annotation { "Feature Type Name" : "Feature", "Feature Type Description" : "" }
export const myFeature = defineFeature(function(context is Context, id is Id, definition is map)
    precondition{}
    {
        {
            var Q0;
            Q0=qCreatedBy(makeId("Top.planeOp"),FACE);
            var sketch = newSketch(context, id + "F0", { "sketchPlane" : qUnion([Q0])});
            skLineSegment(sketch, "E0.bottom", {"start": v(0, 0) * mm, "end": v(9, 0) * mm});
            skLineSegment(sketch, "E0.top", {"start": v(0, -17) * mm, "end": v(9, -17) * mm});
            skLineSegment(sketch, "E0.left", {"start": v(0, 0) * mm, "end": v(0, -17) * mm});
            skLineSegment(sketch, "E0.right", {"start": v(9, 0) * mm, "end": v(9, -17) * mm});
            skSolve(sketch);
        }
        {
            var Q0;
            Q0=makeQuery(id+"F0.imprint","IMPRINT",FACE,{"disambiguationData":[TD([[makeQuery(id+"F0.imprint","IMPRINT",EDGE,{"derivedFrom":sQuery(id+"F0.wireOp",EDGE,"E0.bottom")}),-1.0]])]});
            var Q1;
            Q1=sQuery(id+"F0.wireOp",EDGE,"E0.bottom");
            revolve(context, id + "F1", {"entities" : qUnion([Q0]), "axis" : qUnion([Q1]), "revolveType" : RevolveType.TWO_DIRECTIONS, "angle" : 0.56 * degree, "angleBack" : 0.1 * degree});
        }
        {
            var Q0;
            Q0=makeQuery(id+"F1.opRevolve","SWEPT_EDGE",EDGE,{"disambiguationData":[OSD([sQuery(id+"F0.wireOp",EDGE,"E0.top"),sQuery(id+"F0.wireOp",EDGE,"E0.left")])]});
            var Q1;
            Q1=makeQuery(id+"F1.opRevolve","SWEPT_EDGE",EDGE,{"disambiguationData":[OSD([sQuery(id+"F0.wireOp",EDGE,"E0.top"),sQuery(id+"F0.wireOp",EDGE,"E0.right")])]});
            chamfer(context, id + "F2", {"entities" : qUnion([Q0, Q1]), "chamferType" : ChamferType.OFFSET_ANGLE, "width" : 2 * mm, "oppositeDirection" : false, "angle" : 45 * degree, "tangentPropagation" : true});
        }
        {
            var Q0;
            Q0=sQuery(id+"F0.wireOp",VERTEX,"E0.left.end");
            var Q1;
            Q1=qCreatedBy(makeId("Front.planeOp"),FACE);
            cPlane(context, id + "F3", {"entities" : qUnion([Q0, Q1]), "cplaneType" : CPlaneType.PLANE_POINT, "offset" : 25 * mm, "width" : 150 * mm, "height" : 150 * mm});
        }
        {
            var Q0;
            Q0=qCreatedBy(id+"F3.planeOp",FACE);
            var sketch = newSketch(context, id + "F4", { "sketchPlane" : qUnion([Q0])});
            skLineSegment(sketch, "E1.bottom", {"start": v(2.01, -0.17) * mm, "end": v(2.11, -0.17) * mm});
            skLineSegment(sketch, "E1.top", {"start": v(2.01, -0.07) * mm, "end": v(2.11, -0.07) * mm});
            skLineSegment(sketch, "E1.left", {"start": v(2.01, -0.17) * mm, "end": v(2.01, -0.07) * mm});
            skLineSegment(sketch, "E1.right", {"start": v(2.11, -0.17) * mm, "end": v(2.11, -0.07) * mm});
            skLineSegment(sketch, "E2.bottom", {"start": v(2.11, -0.16) * mm, "end": v(2.21, -0.16) * mm});
            skLineSegment(sketch, "E2.top", {"start": v(2.11, -0.06) * mm, "end": v(2.21, -0.06) * mm});
            skLineSegment(sketch, "E2.left", {"start": v(2.11, -0.16) * mm, "end": v(2.11, -0.06) * mm});
            skLineSegment(sketch, "E2.right", {"start": v(2.21, -0.16) * mm, "end": v(2.21, -0.06) * mm});
            skLineSegment(sketch, "E3.bottom", {"start": v(2.21, -0.14) * mm, "end": v(2.31, -0.14) * mm});
            skLineSegment(sketch, "E3.top", {"start": v(2.21, -0.04) * mm, "end": v(2.31, -0.04) * mm});
            skLineSegment(sketch, "E3.left", {"start": v(2.21, -0.14) * mm, "end": v(2.21, -0.04) * mm});
            skLineSegment(sketch, "E3.right", {"start": v(2.31, -0.14) * mm, "end": v(2.31, -0.04) * mm});
            skLineSegment(sketch, "E4.bottom", {"start": v(2.31, -0.13) * mm, "end": v(2.41, -0.13) * mm});
            skLineSegment(sketch, "E4.top", {"start": v(2.31, -0.03) * mm, "end": v(2.41, -0.03) * mm});
            skLineSegment(sketch, "E4.left", {"start": v(2.31, -0.13) * mm, "end": v(2.31, -0.03) * mm});
            skLineSegment(sketch, "E4.right", {"start": v(2.41, -0.13) * mm, "end": v(2.41, -0.03) * mm});
            skSolve(sketch);
        }
        {
            var Q0;
            Q0=qCreatedBy(id+"F3.planeOp",FACE);
            var sketch = newSketch(context, id + "F5", { "sketchPlane" : qUnion([Q0])});
            skLineSegment(sketch, "E5.bottom", {"start": v(2, -0.1) * mm, "end": v(2.1, -0.1) * mm});
            skLineSegment(sketch, "E5.top", {"start": v(2, -0.2) * mm, "end": v(2.1, -0.2) * mm});
            skLineSegment(sketch, "E5.left", {"start": v(2, -0.1) * mm, "end": v(2, -0.2) * mm});
            skLineSegment(sketch, "E5.right", {"start": v(2.1, -0.1) * mm, "end": v(2.1, -0.2) * mm});
            skLineSegment(sketch, "E6.1.0.0", {"start": v(2.1, -0.1) * mm, "end": v(2.2, -0.1) * mm});
            skLineSegment(sketch, "E6.1.0.1", {"start": v(2.1, -0.2) * mm, "end": v(2.2, -0.2) * mm});
            skLineSegment(sketch, "E6.1.0.3", {"start": v(2.2, -0.1) * mm, "end": v(2.2, -0.2) * mm});
            skLineSegment(sketch, "E6.2.0.0", {"start": v(2.2, -0.09) * mm, "end": v(2.3, -0.09) * mm});
            skLineSegment(sketch, "E6.2.0.1", {"start": v(2.2, -0.19) * mm, "end": v(2.3, -0.19) * mm});
            skLineSegment(sketch, "E6.2.0.2", {"start": v(2.2, -0.09) * mm, "end": v(2.2, -0.19) * mm});
            skLineSegment(sketch, "E6.2.0.3", {"start": v(2.3, -0.09) * mm, "end": v(2.3, -0.19) * mm});
            skLineSegment(sketch, "E6.direction1", {"start": v(2.1, -0.2) * mm, "end": v(2.2, -0.2) * mm, "construction": true});
            skLineSegment(sketch, "E7.0.3.0", {"start": v(2.3, -0.08) * mm, "end": v(2.4, -0.08) * mm});
            skLineSegment(sketch, "E7.3.3.0", {"start": v(2.3, -0.18) * mm, "end": v(2.4, -0.18) * mm});
            skLineSegment(sketch, "E7.6.3.0", {"start": v(2.3, -0.08) * mm, "end": v(2.3, -0.18) * mm});
            skLineSegment(sketch, "E7.9.3.0", {"start": v(2.4, -0.08) * mm, "end": v(2.4, -0.18) * mm});
            skLineSegment(sketch, "E7.0.4.0", {"start": v(2.4, -0.07) * mm, "end": v(2.5, -0.07) * mm});
            skLineSegment(sketch, "E7.3.4.0", {"start": v(2.4, -0.17) * mm, "end": v(2.5, -0.17) * mm});
            skLineSegment(sketch, "E7.6.4.0", {"start": v(2.4, -0.07) * mm, "end": v(2.4, -0.17) * mm});
            skLineSegment(sketch, "E7.9.4.0", {"start": v(2.5, -0.07) * mm, "end": v(2.5, -0.17) * mm});
            skLineSegment(sketch, "E7.0.5.0", {"start": v(2.5, -0.06) * mm, "end": v(2.6, -0.06) * mm});
            skLineSegment(sketch, "E7.3.5.0", {"start": v(2.5, -0.16) * mm, "end": v(2.6, -0.16) * mm});
            skLineSegment(sketch, "E7.6.5.0", {"start": v(2.5, -0.06) * mm, "end": v(2.5, -0.16) * mm});
            skLineSegment(sketch, "E7.9.5.0", {"start": v(2.6, -0.06) * mm, "end": v(2.6, -0.16) * mm});
            skLineSegment(sketch, "E7.0.6.0", {"start": v(2.6, -0.05) * mm, "end": v(2.7, -0.05) * mm});
            skLineSegment(sketch, "E7.3.6.0", {"start": v(2.6, -0.15) * mm, "end": v(2.7, -0.15) * mm});
            skLineSegment(sketch, "E7.6.6.0", {"start": v(2.6, -0.05) * mm, "end": v(2.6, -0.15) * mm});
            skLineSegment(sketch, "E7.9.6.0", {"start": v(2.7, -0.05) * mm, "end": v(2.7, -0.15) * mm});
            skLineSegment(sketch, "E7.0.7.0", {"start": v(2.7, -0.04) * mm, "end": v(2.8, -0.04) * mm});
            skLineSegment(sketch, "E7.3.7.0", {"start": v(2.7, -0.14) * mm, "end": v(2.8, -0.14) * mm});
            skLineSegment(sketch, "E7.6.7.0", {"start": v(2.7, -0.04) * mm, "end": v(2.7, -0.14) * mm});
            skLineSegment(sketch, "E7.9.7.0", {"start": v(2.8, -0.04) * mm, "end": v(2.8, -0.14) * mm});
            skLineSegment(sketch, "E7.0.8.0", {"start": v(2.8, -0.03) * mm, "end": v(2.9, -0.03) * mm});
            skLineSegment(sketch, "E7.3.8.0", {"start": v(2.8, -0.13) * mm, "end": v(2.9, -0.13) * mm});
            skLineSegment(sketch, "E7.6.8.0", {"start": v(2.8, -0.03) * mm, "end": v(2.8, -0.13) * mm});
            skLineSegment(sketch, "E7.9.8.0", {"start": v(2.9, -0.03) * mm, "end": v(2.9, -0.13) * mm});
            skLineSegment(sketch, "E7.0.9.0", {"start": v(2.9, -0.02) * mm, "end": v(3, -0.02) * mm});
            skLineSegment(sketch, "E7.3.9.0", {"start": v(2.9, -0.12) * mm, "end": v(3, -0.12) * mm});
            skLineSegment(sketch, "E7.6.9.0", {"start": v(2.9, -0.02) * mm, "end": v(2.9, -0.12) * mm});
            skLineSegment(sketch, "E7.9.9.0", {"start": v(3, -0.02) * mm, "end": v(3, -0.12) * mm});
            skLineSegment(sketch, "E7.0.10.0", {"start": v(3, 0) * mm, "end": v(3.1, 0) * mm});
            skLineSegment(sketch, "E7.3.10.0", {"start": v(3, -0.1) * mm, "end": v(3.1, -0.1) * mm});
            skLineSegment(sketch, "E7.6.10.0", {"start": v(3, 0) * mm, "end": v(3, -0.1) * mm});
            skLineSegment(sketch, "E7.9.10.0", {"start": v(3.1, 0) * mm, "end": v(3.1, -0.1) * mm});
            skLineSegment(sketch, "E7.0.11.0", {"start": v(3.11, 0) * mm, "end": v(3.21, 0) * mm});
            skLineSegment(sketch, "E7.3.11.0", {"start": v(3.11, -0.1) * mm, "end": v(3.21, -0.1) * mm});
            skLineSegment(sketch, "E7.6.11.0", {"start": v(3.11, 0) * mm, "end": v(3.11, -0.1) * mm});
            skLineSegment(sketch, "E7.9.11.0", {"start": v(3.21, 0) * mm, "end": v(3.21, -0.1) * mm});
            skLineSegment(sketch, "E7.0.12.0", {"start": v(3.21, 0.01) * mm, "end": v(3.31, 0.01) * mm});
            skLineSegment(sketch, "E7.3.12.0", {"start": v(3.21, -0.09) * mm, "end": v(3.31, -0.09) * mm});
            skLineSegment(sketch, "E7.6.12.0", {"start": v(3.21, 0.01) * mm, "end": v(3.21, -0.09) * mm});
            skLineSegment(sketch, "E7.9.12.0", {"start": v(3.31, 0.01) * mm, "end": v(3.31, -0.09) * mm});
            skLineSegment(sketch, "E7.0.13.0", {"start": v(3.31, 0.02) * mm, "end": v(3.41, 0.02) * mm});
            skLineSegment(sketch, "E7.3.13.0", {"start": v(3.31, -0.08) * mm, "end": v(3.41, -0.08) * mm});
            skLineSegment(sketch, "E7.6.13.0", {"start": v(3.31, 0.02) * mm, "end": v(3.31, -0.08) * mm});
            skLineSegment(sketch, "E7.9.13.0", {"start": v(3.41, 0.02) * mm, "end": v(3.41, -0.08) * mm});
            skLineSegment(sketch, "E7.0.14.0", {"start": v(3.41, 0.03) * mm, "end": v(3.51, 0.03) * mm});
            skLineSegment(sketch, "E7.3.14.0", {"start": v(3.41, -0.07) * mm, "end": v(3.51, -0.07) * mm});
            skLineSegment(sketch, "E7.6.14.0", {"start": v(3.41, 0.03) * mm, "end": v(3.41, -0.07) * mm});
            skLineSegment(sketch, "E7.9.14.0", {"start": v(3.51, 0.03) * mm, "end": v(3.51, -0.07) * mm});
            skLineSegment(sketch, "E7.0.15.0", {"start": v(3.51, 0.04) * mm, "end": v(3.61, 0.04) * mm});
            skLineSegment(sketch, "E7.3.15.0", {"start": v(3.51, -0.06) * mm, "end": v(3.61, -0.06) * mm});
            skLineSegment(sketch, "E7.6.15.0", {"start": v(3.51, 0.04) * mm, "end": v(3.51, -0.06) * mm});
            skLineSegment(sketch, "E7.9.15.0", {"start": v(3.61, 0.04) * mm, "end": v(3.61, -0.06) * mm});
            skLineSegment(sketch, "E7.0.16.0", {"start": v(3.62, 0.05) * mm, "end": v(3.72, 0.05) * mm});
            skLineSegment(sketch, "E7.3.16.0", {"start": v(3.62, -0.05) * mm, "end": v(3.72, -0.05) * mm});
            skLineSegment(sketch, "E7.6.16.0", {"start": v(3.62, 0.05) * mm, "end": v(3.62, -0.05) * mm});
            skLineSegment(sketch, "E7.9.16.0", {"start": v(3.72, 0.05) * mm, "end": v(3.72, -0.05) * mm});
            skLineSegment(sketch, "E7.0.17.0", {"start": v(3.72, 0.06) * mm, "end": v(3.82, 0.06) * mm});
            skLineSegment(sketch, "E7.3.17.0", {"start": v(3.72, -0.04) * mm, "end": v(3.82, -0.04) * mm});
            skLineSegment(sketch, "E7.6.17.0", {"start": v(3.72, 0.06) * mm, "end": v(3.72, -0.04) * mm});
            skLineSegment(sketch, "E7.9.17.0", {"start": v(3.82, 0.06) * mm, "end": v(3.82, -0.04) * mm});
            skLineSegment(sketch, "E7.0.18.0", {"start": v(3.82, 0.07) * mm, "end": v(3.92, 0.07) * mm});
            skLineSegment(sketch, "E7.3.18.0", {"start": v(3.82, -0.03) * mm, "end": v(3.92, -0.03) * mm});
            skLineSegment(sketch, "E7.6.18.0", {"start": v(3.82, 0.07) * mm, "end": v(3.82, -0.03) * mm});
            skLineSegment(sketch, "E7.9.18.0", {"start": v(3.92, 0.07) * mm, "end": v(3.92, -0.03) * mm});
            skLineSegment(sketch, "E7.0.19.0", {"start": v(3.92, 0.08) * mm, "end": v(4.02, 0.08) * mm});
            skLineSegment(sketch, "E7.3.19.0", {"start": v(3.92, -0.02) * mm, "end": v(4.02, -0.02) * mm});
            skLineSegment(sketch, "E7.6.19.0", {"start": v(3.92, 0.08) * mm, "end": v(3.92, -0.02) * mm});
            skLineSegment(sketch, "E7.9.19.0", {"start": v(4.02, 0.08) * mm, "end": v(4.02, -0.02) * mm});
            skSolve(sketch);
        }
        {
            var Q0;
            Q0=makeQuery(id+"F4.imprint","IMPRINT",FACE,{"disambiguationData":[TD([[makeQuery(id+"F4.imprint","IMPRINT",EDGE,{"derivedFrom":sQuery(id+"F4.wireOp",EDGE,"E1.bottom")}),1.0]])]});
            extrude(context, id + "F6", {"entities" : qUnion([Q0]), "operationType" : NewBodyOperationType.REMOVE, "oppositeDirection" : true, "depth" : 0.1 * mm, "hasDraft" : true, "draftAngle" : 30 * degree, "draftPullDirection" : true});
        }
        {
            var Q0;
            {var subQ3=sQuery(id+"F4.wireOp",EDGE,"E2.bottom");Q0=makeQuery(id+"F4.imprint","IMPRINT",FACE,{"disambiguationData":[TD([[makeQuery(id+"F4.imprint","IMPRINT",EDGE,{"derivedFrom":subQ3}),1.0]])]});}
            extrude(context, id + "F7", {"entities" : qUnion([Q0]), "operationType" : NewBodyOperationType.REMOVE, "oppositeDirection" : true, "depth" : 0.1 * mm, "hasDraft" : true, "draftAngle" : 30 * degree, "draftPullDirection" : true});
        }
        {
            var Q0;
            {var subQ3=sQuery(id+"F4.wireOp",EDGE,"E4.bottom");Q0=makeQuery(id+"F4.imprint","IMPRINT",FACE,{"disambiguationData":[TD([[makeQuery(id+"F4.imprint","IMPRINT",EDGE,{"derivedFrom":subQ3}),1.0]])]});}
            extrude(context, id + "F8", {"entities" : qUnion([Q0]), "operationType" : NewBodyOperationType.REMOVE, "oppositeDirection" : true, "depth" : 0.1 * mm, "hasDraft" : true, "draftAngle" : 30 * degree, "draftPullDirection" : true});
        }
        {
            var Q0;
            {var subQ3=sQuery(id+"F4.wireOp",EDGE,"E3.bottom");Q0=makeQuery(id+"F4.imprint","IMPRINT",FACE,{"disambiguationData":[TD([[makeQuery(id+"F4.imprint","IMPRINT",EDGE,{"derivedFrom":subQ3}),1.0]])]});}
            extrude(context, id + "F9", {"entities" : qUnion([Q0]), "operationType" : NewBodyOperationType.REMOVE, "oppositeDirection" : true, "depth" : 0.1 * mm, "hasDraft" : true, "draftAngle" : 30 * degree, "draftPullDirection" : true});
        }
        {
            var Q0;
            Q0=makeQuery(id+"F1.opRevolve","SWEPT_BODY",BODY,{"disambiguationData":[OSD([sQuery(id+"F0.wireOp",EDGE,"E0.bottom"),sQuery(id+"F0.wireOp",EDGE,"E0.top"),sQuery(id+"F0.wireOp",EDGE,"E0.left"),sQuery(id+"F0.wireOp",EDGE,"E0.right")])]});
            var Q1;
            Q1=sQuery(id+"F0.wireOp",EDGE,"E0.bottom");
            circularPattern(context, id + "F10", {"operationType" : NewBodyOperationType.ADD, "entities" : qUnion([Q0]), "axis" : qUnion([Q1]), "angle" : 360 * degree, "instanceCount" : 360, "equalSpace" : true, "computeTransformsWithoutBuiltin" : true});
        }
        {
            var Q0;
            Q0=makeQuery(id+"F5.imprint","IMPRINT",FACE,{"disambiguationData":[TD([[makeQuery(id+"F5.imprint","IMPRINT",EDGE,{"derivedFrom":sQuery(id+"F5.wireOp",EDGE,"E5.bottom")}),-1.0]])]});
            var Q1;
            Q1=makeQuery(id+"F5.imprint","IMPRINT",FACE,{"disambiguationData":[TD([[makeQuery(id+"F5.imprint","IMPRINT",EDGE,{"derivedFrom":sQuery(id+"F5.wireOp",EDGE,"E6.1.0.0")}),-1.0]])]});
            var Q2;
            Q2=makeQuery(id+"F5.imprint","IMPRINT",FACE,{"disambiguationData":[TD([[makeQuery(id+"F5.imprint","IMPRINT",EDGE,{"derivedFrom":sQuery(id+"F5.wireOp",EDGE,"E6.2.0.0")}),-1.0]])]});
            var Q3;
            Q3=makeQuery(id+"F5.imprint","IMPRINT",FACE,{"disambiguationData":[TD([[makeQuery(id+"F5.imprint","IMPRINT",EDGE,{"derivedFrom":sQuery(id+"F5.wireOp",EDGE,"E7.0.3.0")}),-1.0]])]});
            var Q4;
            Q4=makeQuery(id+"F5.imprint","IMPRINT",FACE,{"disambiguationData":[TD([[makeQuery(id+"F5.imprint","IMPRINT",EDGE,{"derivedFrom":sQuery(id+"F5.wireOp",EDGE,"E7.0.4.0")}),-1.0]])]});
            var Q5;
            Q5=makeQuery(id+"F5.imprint","IMPRINT",FACE,{"disambiguationData":[TD([[makeQuery(id+"F5.imprint","IMPRINT",EDGE,{"derivedFrom":sQuery(id+"F5.wireOp",EDGE,"E7.0.5.0")}),-1.0]])]});
            var Q6;
            Q6=makeQuery(id+"F5.imprint","IMPRINT",FACE,{"disambiguationData":[TD([[makeQuery(id+"F5.imprint","IMPRINT",EDGE,{"derivedFrom":sQuery(id+"F5.wireOp",EDGE,"E7.0.6.0")}),-1.0]])]});
            var Q7;
            Q7=makeQuery(id+"F5.imprint","IMPRINT",FACE,{"disambiguationData":[TD([[makeQuery(id+"F5.imprint","IMPRINT",EDGE,{"derivedFrom":sQuery(id+"F5.wireOp",EDGE,"E7.0.7.0")}),-1.0]])]});
            var Q8;
            Q8=makeQuery(id+"F5.imprint","IMPRINT",FACE,{"disambiguationData":[TD([[makeQuery(id+"F5.imprint","IMPRINT",EDGE,{"derivedFrom":sQuery(id+"F5.wireOp",EDGE,"E7.0.8.0")}),-1.0]])]});
            var Q9;
            Q9=makeQuery(id+"F5.imprint","IMPRINT",FACE,{"disambiguationData":[TD([[makeQuery(id+"F5.imprint","IMPRINT",EDGE,{"derivedFrom":sQuery(id+"F5.wireOp",EDGE,"E7.0.9.0")}),-1.0]])]});
            var Q10;
            Q10=makeQuery(id+"F5.imprint","IMPRINT",FACE,{"disambiguationData":[TD([[makeQuery(id+"F5.imprint","IMPRINT",EDGE,{"derivedFrom":sQuery(id+"F5.wireOp",EDGE,"E7.0.10.0")}),-1.0]])]});
            var Q11;
            Q11=makeQuery(id+"F5.imprint","IMPRINT",FACE,{"disambiguationData":[TD([[makeQuery(id+"F5.imprint","IMPRINT",EDGE,{"derivedFrom":sQuery(id+"F5.wireOp",EDGE,"E7.0.11.0")}),-1.0]])]});
            var Q12;
            Q12=makeQuery(id+"F5.imprint","IMPRINT",FACE,{"disambiguationData":[TD([[makeQuery(id+"F5.imprint","IMPRINT",EDGE,{"derivedFrom":sQuery(id+"F5.wireOp",EDGE,"E7.0.12.0")}),-1.0]])]});
            var Q13;
            Q13=makeQuery(id+"F5.imprint","IMPRINT",FACE,{"disambiguationData":[TD([[makeQuery(id+"F5.imprint","IMPRINT",EDGE,{"derivedFrom":sQuery(id+"F5.wireOp",EDGE,"E7.0.13.0")}),-1.0]])]});
            var Q14;
            Q14=makeQuery(id+"F5.imprint","IMPRINT",FACE,{"disambiguationData":[TD([[makeQuery(id+"F5.imprint","IMPRINT",EDGE,{"derivedFrom":sQuery(id+"F5.wireOp",EDGE,"E7.0.16.0")}),-1.0]])]});
            var Q15;
            Q15=makeQuery(id+"F5.imprint","IMPRINT",FACE,{"disambiguationData":[TD([[makeQuery(id+"F5.imprint","IMPRINT",EDGE,{"derivedFrom":sQuery(id+"F5.wireOp",EDGE,"E7.0.18.0")}),-1.0]])]});
            var Q16;
            Q16=makeQuery(id+"F5.imprint","IMPRINT",FACE,{"disambiguationData":[TD([[makeQuery(id+"F5.imprint","IMPRINT",EDGE,{"derivedFrom":sQuery(id+"F5.wireOp",EDGE,"E7.0.19.0")}),-1.0]])]});
            var Q17;
            Q17=makeQuery(id+"F5.imprint","IMPRINT",FACE,{"disambiguationData":[TD([[makeQuery(id+"F5.imprint","IMPRINT",EDGE,{"derivedFrom":sQuery(id+"F5.wireOp",EDGE,"E7.0.14.0")}),-1.0]])]});
            var Q18;
            Q18=makeQuery(id+"F5.imprint","IMPRINT",FACE,{"disambiguationData":[TD([[makeQuery(id+"F5.imprint","IMPRINT",EDGE,{"derivedFrom":sQuery(id+"F5.wireOp",EDGE,"E7.0.15.0")}),-1.0]])]});
            var Q19;
            Q19=makeQuery(id+"F5.imprint","IMPRINT",FACE,{"disambiguationData":[TD([[makeQuery(id+"F5.imprint","IMPRINT",EDGE,{"derivedFrom":sQuery(id+"F5.wireOp",EDGE,"E7.0.17.0")}),-1.0]])]});
            extrude(context, id + "F11", {"entities" : qUnion([Q0, Q1, Q2, Q3, Q4, Q5, Q6, Q7, Q8, Q9, Q10, Q11, Q12, Q13, Q14, Q15, Q16, Q17, Q18, Q19]), "operationType" : NewBodyOperationType.REMOVE, "oppositeDirection" : true, "depth" : 0.1 * mm, "hasDraft" : true, "draftAngle" : 30 * degree, "draftPullDirection" : true});
        }
    });